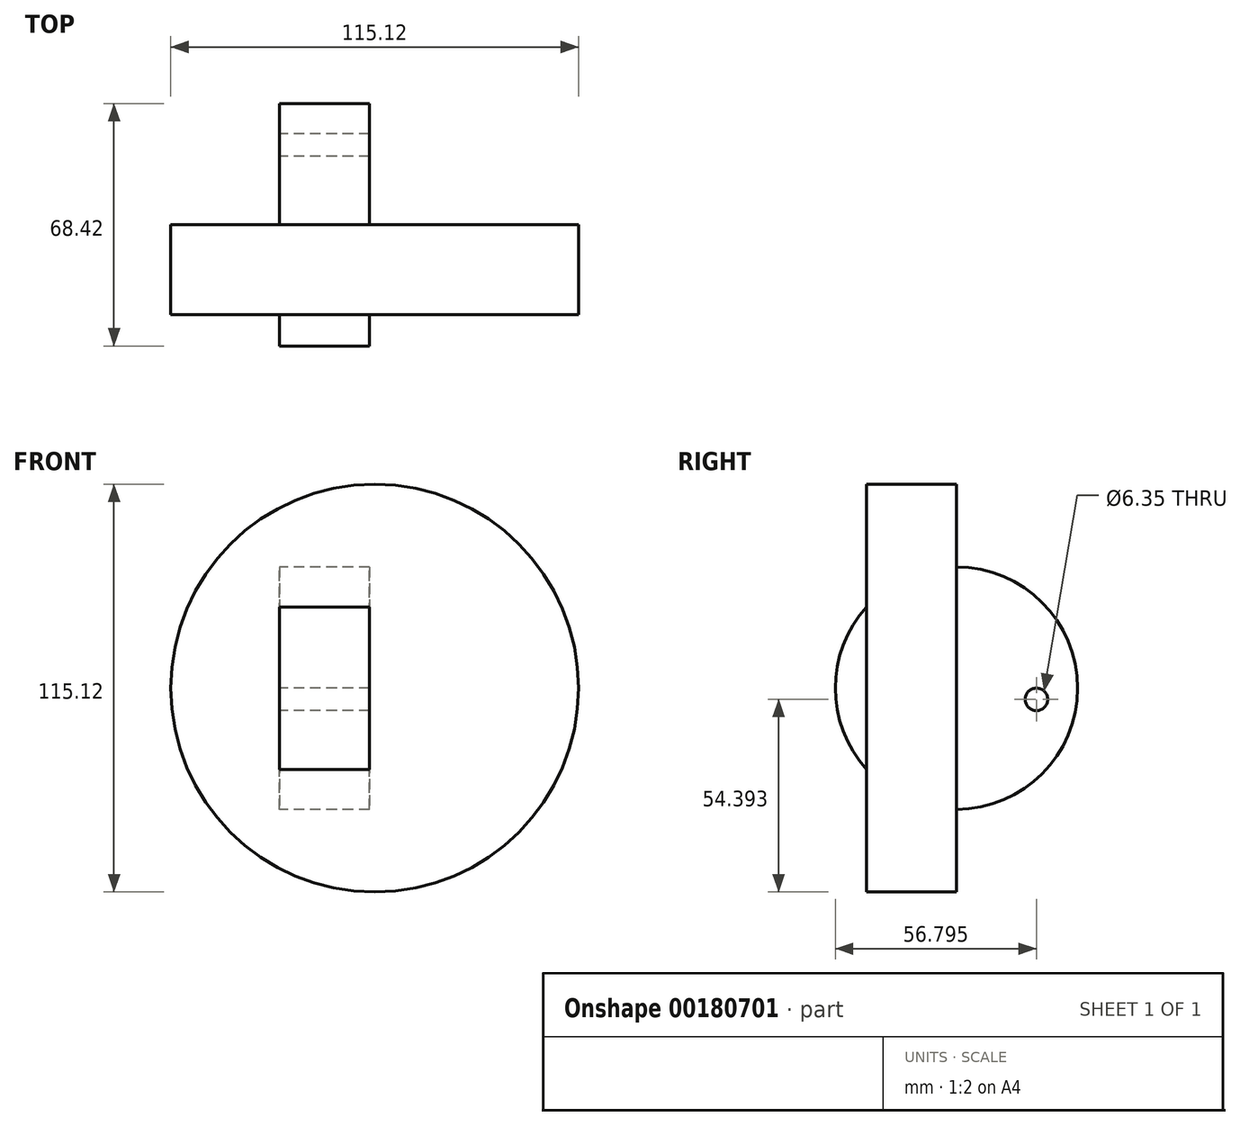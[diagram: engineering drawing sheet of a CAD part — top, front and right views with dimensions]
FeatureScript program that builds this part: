
annotation { "Feature Type Name" : "Feature", "Feature Type Description" : "" }
export const myFeature = defineFeature(function(context is Context, id is Id, definition is map)
    precondition{}
    {
        {
            var Q0;
            Q0=qCreatedBy(makeId("Right.planeOp"),FACE);
            var sketch = newSketch(context, id + "F0", { "sketchPlane" : qUnion([Q0])});
            skCircle(sketch, "E0", {"center": v(0, 0) * mm, "radius": 34.21 * mm});
            skSolve(sketch);
        }
        {
            var Q0;
            Q0 = qSketchRegion(id + "F0", true);
            extrude(context, id + "F1", {"entities" : qUnion([Q0]), "depth" : 25.4 * mm});
        }
        {
            var Q0;
            Q0=qCreatedBy(makeId("Front.planeOp"),FACE);
            var sketch = newSketch(context, id + "F2", { "sketchPlane" : qUnion([Q0])});
            skCircle(sketch, "E1", {"center": v(26.85, 0) * mm, "radius": 57.56 * mm});
            skSolve(sketch);
        }
        {
            var Q0;
            Q0 = qSketchRegion(id + "F2", true);
            extrude(context, id + "F3", {"entities" : qUnion([Q0]), "operationType" : NewBodyOperationType.ADD, "depth" : 25.4 * mm});
        }
        {
            var Q0;
            Q0=qCreatedBy(makeId("Right.planeOp"),FACE);
            var sketch = newSketch(context, id + "F4", { "sketchPlane" : qUnion([Q0])});
            skCircle(sketch, "E2", {"center": v(22.58, -3.17) * mm, "radius": 37.58 * mm});
            skSolve(sketch);
        }
        {
            var Q0;
            Q0=sQuery(id+"F4.wireOp",VERTEX,"E2.center");
            var Q1;
            Q1=makeQuery(id+"F1.opExtrude","SWEPT_BODY",BODY,{"disambiguationData":[OSD([sQuery(id+"F0.wireOp",EDGE,"E0")])]});
            hole(context, id + "F5", {"style" : HoleStyle.SIMPLE, "endStyle" : HoleEndStyle.THROUGH, "oppositeDirection" : true, "holeDiameter" : 6.35 * mm, "locations" : qUnion([Q0]), "scope" : qUnion([Q1]), "isTappedThrough" : true});
        }
    });
